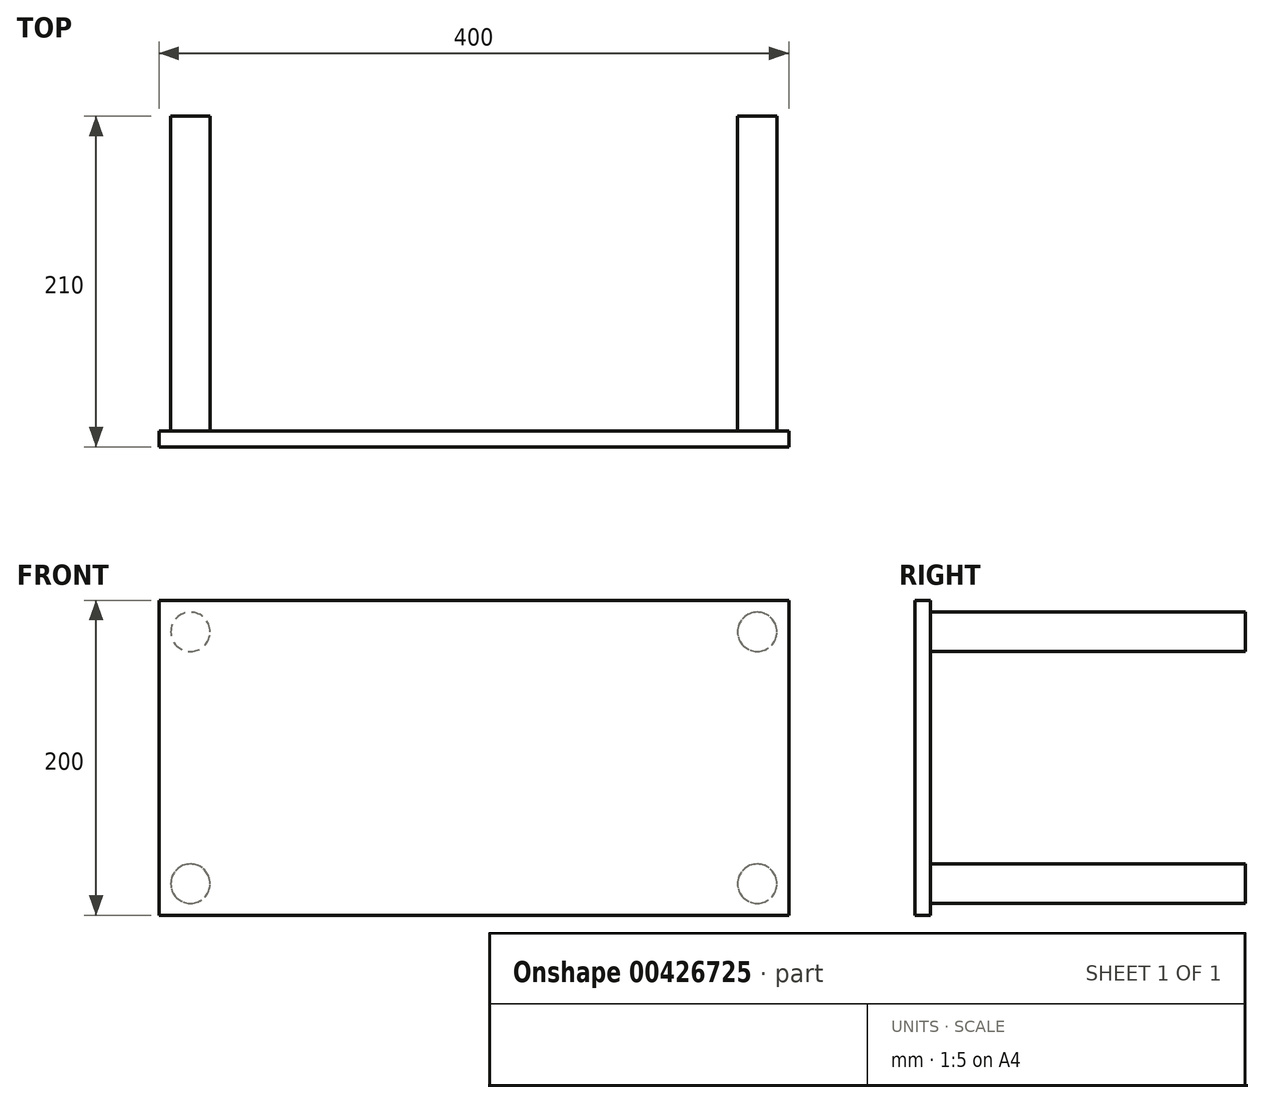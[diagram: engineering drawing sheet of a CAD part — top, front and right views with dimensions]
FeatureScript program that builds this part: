
annotation { "Feature Type Name" : "Feature", "Feature Type Description" : "" }
export const myFeature = defineFeature(function(context is Context, id is Id, definition is map)
    precondition{}
    {
        {
            var Q0;
            Q0=qCreatedBy(makeId("Front.planeOp"),FACE);
            var sketch = newSketch(context, id + "F0", { "sketchPlane" : qUnion([Q0])});
            skLineSegment(sketch, "E0.bottom", {"start": v(-215.9, 73.94) * mm, "end": v(184.1, 73.94) * mm});
            skLineSegment(sketch, "E0.top", {"start": v(-215.9, -126.06) * mm, "end": v(184.1, -126.06) * mm});
            skLineSegment(sketch, "E0.left", {"start": v(-215.9, 73.94) * mm, "end": v(-215.9, -126.06) * mm});
            skLineSegment(sketch, "E0.right", {"start": v(184.1, 73.94) * mm, "end": v(184.1, -126.06) * mm});
            skSolve(sketch);
        }
        {
            var Q0;
            Q0 = qSketchRegion(id + "F0", true);
            extrude(context, id + "F1", {"entities" : qUnion([Q0]), "depth" : 10 * mm});
        }
        {
            var Q0;
            Q0=qCreatedBy(makeId("Front.planeOp"),FACE);
            var sketch = newSketch(context, id + "F2", { "sketchPlane" : qUnion([Q0])});
            skCircle(sketch, "E1", {"center": v(-195.9, 53.94) * mm, "radius": 12.5 * mm});
            skSolve(sketch);
        }
        {
            var Q0;
            Q0 = qSketchRegion(id + "F2", true);
            extrude(context, id + "F3", {"entities" : qUnion([Q0]), "operationType" : NewBodyOperationType.ADD, "oppositeDirection" : true, "depth" : 200 * mm});
        }
        {
            var Q0;
            Q0=makeQuery(id+"F1.opExtrude","CAP_FACE",FACE,{"disambiguationData":[OSD([sQuery(id+"F0.wireOp",EDGE,"E0.bottom"),sQuery(id+"F0.wireOp",EDGE,"E0.top"),sQuery(id+"F0.wireOp",EDGE,"E0.left"),sQuery(id+"F0.wireOp",EDGE,"E0.right")])],"isStart":true});
            var sketch = newSketch(context, id + "F4", { "sketchPlane" : qUnion([Q0])});
            skCircle(sketch, "E2", {"center": v(-164.1, 53.94) * mm, "radius": 12.5 * mm});
            skCircle(sketch, "E3", {"center": v(-164.1, -106.06) * mm, "radius": 12.5 * mm});
            skCircle(sketch, "E4", {"center": v(195.9, -106.06) * mm, "radius": 12.5 * mm});
            skSolve(sketch);
        }
        {
            var Q0;
            Q0 = qSketchRegion(id + "F4", true);
            extrude(context, id + "F5", {"entities" : qUnion([Q0]), "operationType" : NewBodyOperationType.ADD, "depth" : 200 * mm});
        }
    });
